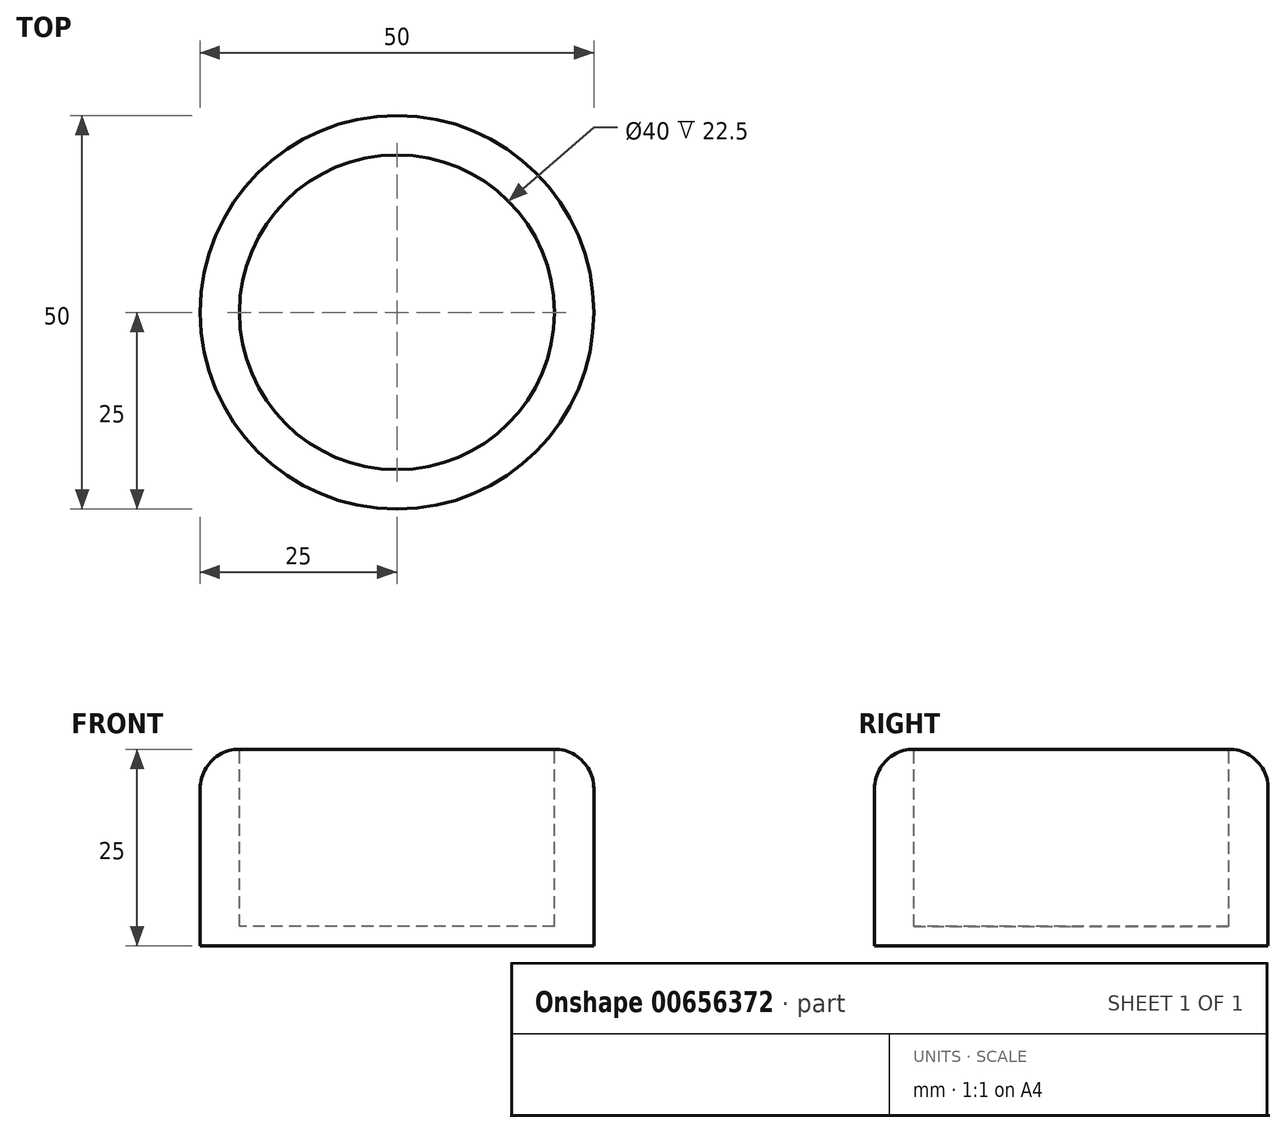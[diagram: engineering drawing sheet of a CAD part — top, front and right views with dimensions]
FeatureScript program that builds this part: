
annotation { "Feature Type Name" : "Feature", "Feature Type Description" : "" }
export const myFeature = defineFeature(function(context is Context, id is Id, definition is map)
    precondition{}
    {
        {
            var Q0;
            Q0=qCreatedBy(makeId("Top.planeOp"),FACE);
            var sketch = newSketch(context, id + "F0", { "sketchPlane" : qUnion([Q0])});
            skCircle(sketch, "E0", {"center": v(0, 0) * mm, "radius": 25 * mm});
            skSolve(sketch);
        }
        {
            var Q0;
            Q0=makeQuery(id+"F0.imprint","IMPRINT",FACE,{"disambiguationData":[TD([[makeQuery(id+"F0.imprint","IMPRINT",EDGE,{"derivedFrom":sQuery(id+"F0.wireOp",EDGE,"E0")}),1.0]])]});
            extrude(context, id + "F1", {"entities" : qUnion([Q0]), "depth" : 25 * mm, "offsetDistance" : 25 * mm});
        }
        {
            var Q0;
            Q0=makeQuery(id+"F1.opExtrude","CAP_EDGE",EDGE,{"disambiguationData":[OSD([sQuery(id+"F0.wireOp",EDGE,"E0")])],"isStart":false});
            fillet(context, id + "F2", {"entities" : qUnion([Q0]), "radius" : 5 * mm, "tangentPropagation" : true, "allowEdgeOverflow" : false});
        }
        {
            var Q0;
            Q0=makeQuery(id+"F1.opExtrude","CAP_FACE",FACE,{"disambiguationData":[OSD([sQuery(id+"F0.wireOp",EDGE,"E0")])],"isStart":false});
            extrude(context, id + "F3", {"entities" : qUnion([Q0]), "operationType" : NewBodyOperationType.ADD, "oppositeDirection" : true, "depth" : 20 * mm, "offsetDistance" : 25 * mm});
        }
        {
            var Q0;
            Q0=makeQuery(id+"F1.opExtrude","CAP_FACE",FACE,{"disambiguationData":[OSD([sQuery(id+"F0.wireOp",EDGE,"E0")])],"isStart":false});
            var sketch = newSketch(context, id + "F4", { "sketchPlane" : qUnion([Q0])});
            skCircle(sketch, "E1", {"center": v(0, 0) * mm, "radius": 20 * mm});
            skSolve(sketch);
        }
        {
            var Q0;
            Q0=makeQuery(id+"F4.imprint","IMPRINT",FACE,{"disambiguationData":[TD([[makeQuery(id+"F4.imprint","IMPRINT",EDGE,{"derivedFrom":sQuery(id+"F4.wireOp",EDGE,"E1")}),1.0]])]});
            var Q1;
            Q1 = qSketchRegion(id + "F4", true);
            extrude(context, id + "F5", {"entities" : qUnion([Q0, Q1]), "operationType" : NewBodyOperationType.REMOVE, "oppositeDirection" : true, "depth" : 22.5 * mm, "offsetDistance" : 25 * mm});
        }
    });
